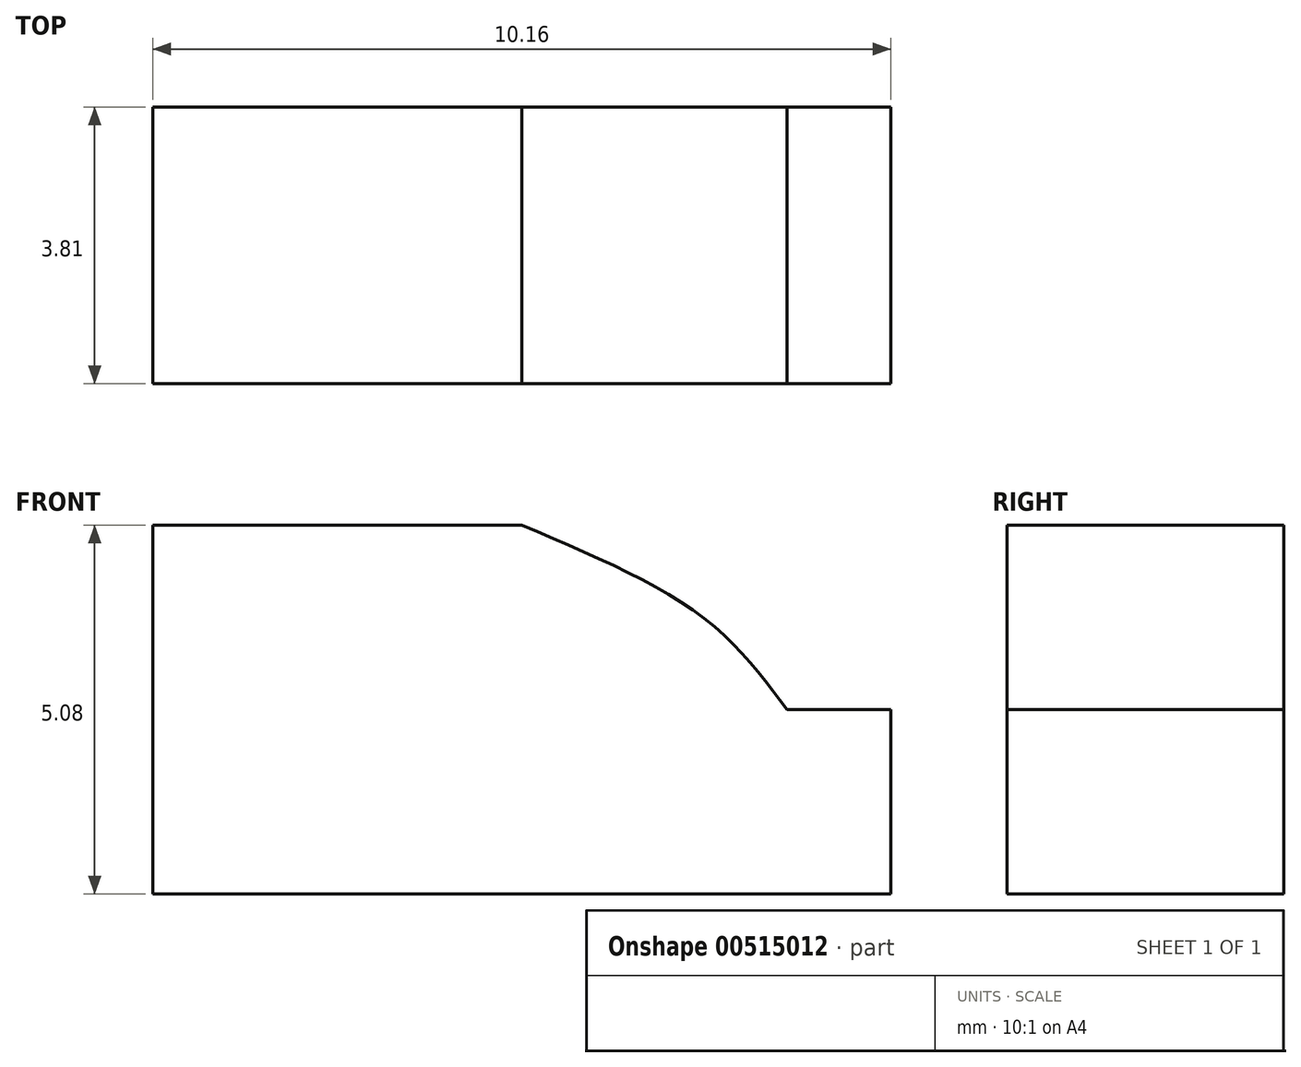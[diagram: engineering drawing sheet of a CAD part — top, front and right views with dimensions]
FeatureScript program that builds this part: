
annotation { "Feature Type Name" : "Feature", "Feature Type Description" : "" }
export const myFeature = defineFeature(function(context is Context, id is Id, definition is map)
    precondition{}
    {
        {
            var Q0;
            Q0=qCreatedBy(makeId("Front.planeOp"),FACE);
            var sketch = newSketch(context, id + "F0", { "sketchPlane" : qUnion([Q0])});
            skLineSegment(sketch, "E0.bottom", {"start": v(-5.08, -2.54) * mm, "end": v(5.08, -2.54) * mm});
            skLineSegment(sketch, "E0.top", {"start": v(-5.08, 2.54) * mm, "end": v(0, 2.54) * mm});
            skLineSegment(sketch, "E0.left", {"start": v(-5.08, 0) * mm, "end": v(-5.08, 2.54) * mm});
            skLineSegment(sketch, "E0.right", {"start": v(5.08, -2.54) * mm, "end": v(5.08, 0) * mm});
            skPoint(sketch, "E0.middle", {"position": v(0, 0) * mm});
            skLineSegment(sketch, "E1", {"start": v(3.65, 0) * mm, "end": v(5.08, 0) * mm});
            skLineSegment(sketch, "E2", {"start": v(0, 0) * mm, "end": v(0, 2.54) * mm});
            skLineSegment(sketch, "E3", {"start": v(0, 2.54) * mm, "end": v(0, 2.54) * mm});
            skPoint(sketch, "E4.start.orphan", {"position": v(2.54, 2.54) * mm});
            skPoint(sketch, "E5.start.orphan", {"position": v(5.08, 2.54) * mm});
            skPoint(sketch, "E6.start.orphan", {"position": v(5.08, 1.27) * mm});
            skFitSpline(sketch, "E7", {"points": [v(0, 2.54) * mm, v(2.5, 1.27) * mm, v(3.65, 0) * mm], "startDerivative": vector(4.95, -2.09) * mm, "endDerivative": vector(2.23, -3.03) * mm});
            skPoint(sketch, "E8.start.orphan", {"position": v(-5.08, 0) * mm});
            skLineSegment(sketch, "E9", {"start": v(-5.08, 0) * mm, "end": v(-5.08, -2.54) * mm});
            skSolve(sketch);
        }
        {
            var Q0;
            Q0 = qSketchRegion(id + "F0", true);
            var Q1;
            Q1=makeQuery(id+"F0.imprint","IMPRINT",FACE,{"disambiguationData":[TD([[makeQuery(id+"F0.imprint","IMPRINT",EDGE,{"derivedFrom":sQuery(id+"F0.wireOp",EDGE,"E0.bottom")}),1.0]])]});
            extrude(context, id + "F1", {"entities" : qUnion([Q0, Q1]), "depth" : 3.8 * mm, "offsetDistance" : 25.4 * mm});
        }
    });
